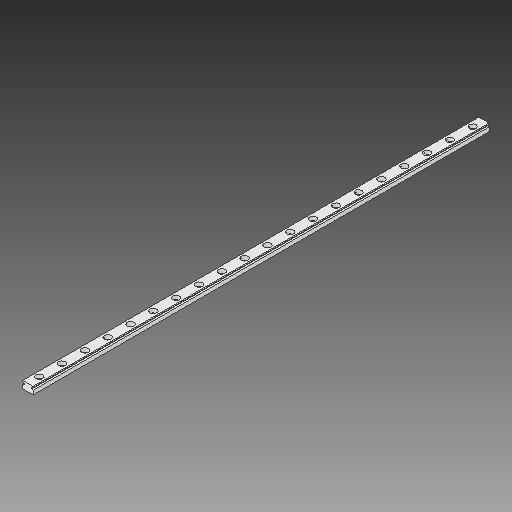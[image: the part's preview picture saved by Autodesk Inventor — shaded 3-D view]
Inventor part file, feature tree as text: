
AUTODESK INVENTOR PART (.ipt)
format: ipt  version: 2019 (Build 230136000, 136)  size: 195,584 bytes
history: mixed  units: mm
features: thicken_offset x2, extrude x2, pattern_linear x2, sketch x2, other x1, imported_body x1
ambient origin geometry x8: Origin, YZ Plane, XZ Plane, XY Plane, X Axis, Y Axis, Z Axis, Center Point
bodies: Solid1 (imported_parasolid)
feature tree (10):
  thicken_offset  "Thicken1"
  extrude  "Extrusion1"  Depth=145.0mm
  pattern_linear  "Rectangular Pattern1"  Spacing1=4.5mm  [1 undecoded]
  extrude  "Extrusion2"  Depth=10.0mm TaperAngle=0.0deg
  pattern_linear  "Rectangular Pattern2"  Count1=7  [1 undecoded]
  thicken_offset  "Thicken2"
  sketch  "Sketch1"  dims[d0=145.0mm d1=150.0mm d2=20.0mm]
  sketch  "Sketch2"  dims[d3=3.5mm d4=4.5mm d5=10.0mm d6=0.0mm d7=70.0mm d9=20.0mm d10=6.0mm d11=3.5mm d12=0.0mm d13=70.0mm d15=20.0mm d16=5.0mm d17=5.0mm]
  other  "LPattern1"
  imported_body  NMx_Import_Brep_tag  [imported B-rep: ~78 faces, bbox_mm=[9.0, 6.5, 400.0]]
note: 2 required parameter values undecoded (feature->parameter linkage not recoverable at this tier; creation-order binding heuristic only, values carry confidence <= 0.55)
